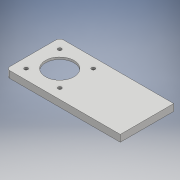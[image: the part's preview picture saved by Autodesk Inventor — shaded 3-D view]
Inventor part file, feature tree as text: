
AUTODESK INVENTOR PART (.ipt)
format: ipt  version: 2018 (Build 220112000, 112)  size: 157,696 bytes
history: native  units: mm
features: other x6, extrude x3, sketch x3, fillet x2
ambient origin geometry x8: Origin, YZ Plane, XZ Plane, XY Plane, X Axis, Y Axis, Z Axis, Center Point
bodies: Body1 (feature_tree)
feature tree (14):
  other  "Sólido1"
  extrude  "Extrusão1"  Depth=160.0mm
  extrude  "Extrusão6"  Depth=9.52mm TaperAngle=0.0deg
  extrude  "Extrusão7"  Depth=59.0mm
  fillet  "Arredondamento1"  Radius=5.0mm
  fillet  "Arredondamento2"  Radius=5.0mm
  sketch  "Esboço1"  dims[d0=160.0mm d1=160.0mm]
  other  "Referência1"
  other  "Referência2"
  sketch  "Esboço9"  dims[d2=75.0mm d3=9.52mm d4=0.0mm]
  sketch  "Esboço10"  dims[d72=59.0mm d73=59.0mm d74=5.0mm d75=5.0mm d76=5.0mm d77=5.0mm d78=23.57mm d79=23.57mm d80=23.57mm d81=23.57mm d82=23.57mm d83=23.57mm d84=23.57mm d85=23.57mm d86=8.0mm d87=8.0mm d88=40.0mm d89=6.52mm d90=0.0mm d91=6.52mm d92=0.0mm d93=6.0mm d94=5.0mm]
  other  "<userpath>\Documents\OpenCNC\MONTAGEM\CNC1.iam"
  other  "CNC1.iam"
  other  "PERFIL_ESTRUTURAL_40X80_EIXO_Y:1"
